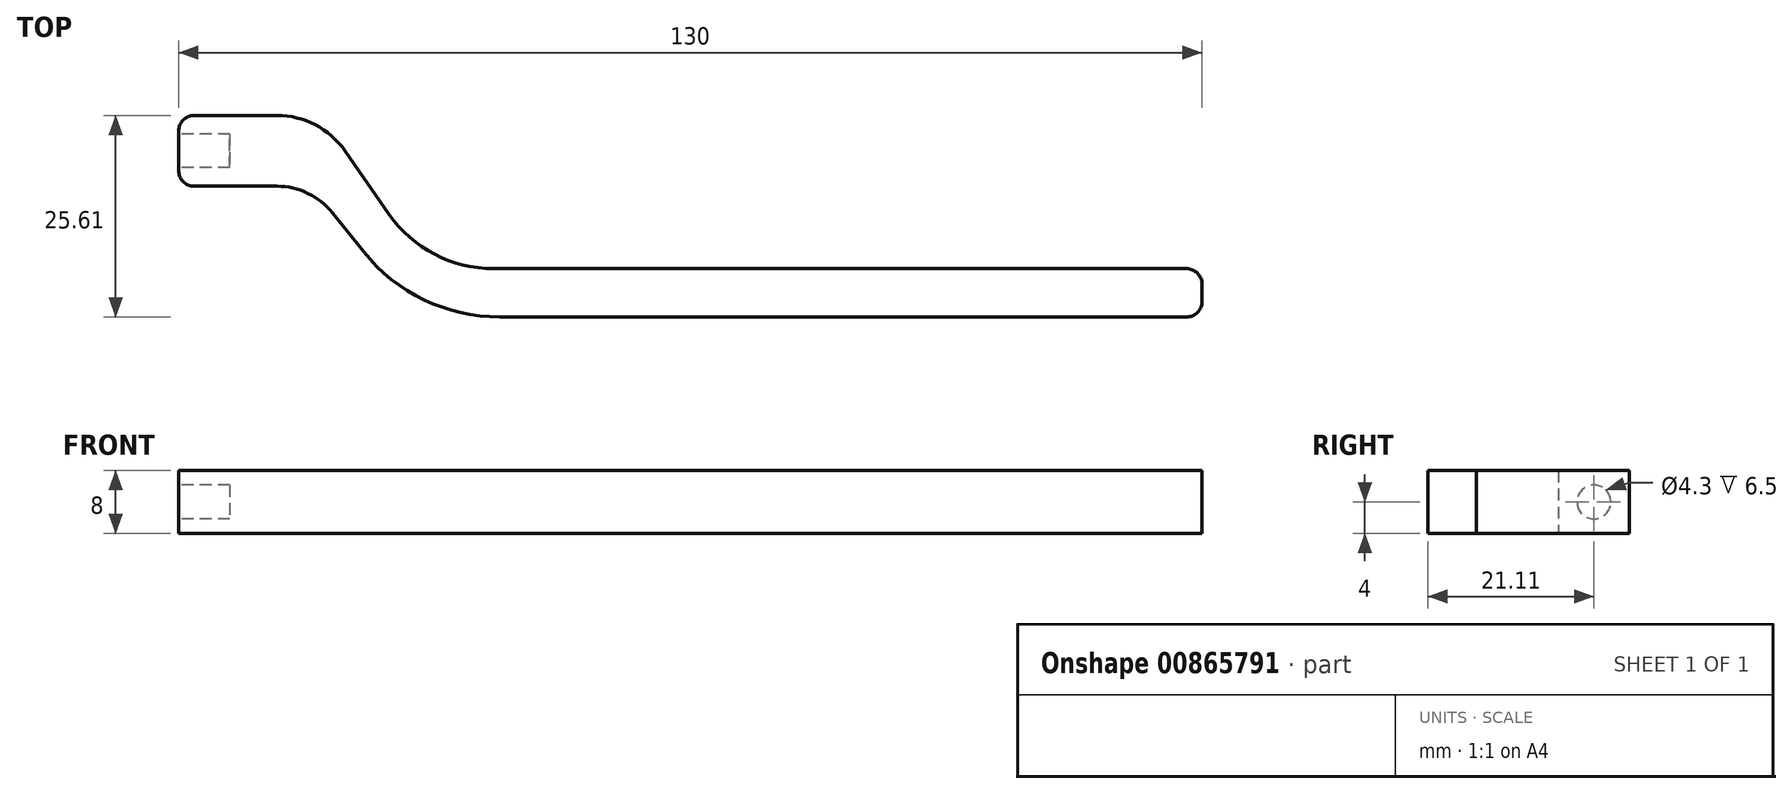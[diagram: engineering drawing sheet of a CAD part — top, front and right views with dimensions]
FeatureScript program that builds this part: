
annotation { "Feature Type Name" : "Feature", "Feature Type Description" : "" }
export const myFeature = defineFeature(function(context is Context, id is Id, definition is map)
    precondition{}
    {
        {
            var Q0;
            Q0=qCreatedBy(makeId("Top.planeOp"),FACE);
            var sketch = newSketch(context, id + "F0", { "sketchPlane" : qUnion([Q0])});
            skLineSegment(sketch, "E0.bottom", {"start": v(6.25, 4.5) * mm, "end": v(-6.25, 4.5) * mm});
            skLineSegment(sketch, "E0.top", {"start": v(6.25, -4.5) * mm, "end": v(-6.25, -4.5) * mm});
            skLineSegment(sketch, "E0.left", {"start": v(6.25, 4.5) * mm, "end": v(6.25, -4.5) * mm});
            skLineSegment(sketch, "E0.right", {"start": v(-6.25, 4.5) * mm, "end": v(-6.25, -4.5) * mm});
            skPoint(sketch, "E0.middle", {"position": v(0, 0) * mm});
            skArc(sketch, "E1", {"start": v(6.25, -4.5) * mm, "mid": v(10.17, -5.4) * mm, "end": v(13.31, -7.9) * mm});
            skLineSegment(sketch, "E2", {"start": v(13.31, -7.9) * mm, "end": v(17.23, -12.8) * mm});
            skArc(sketch, "E3", {"start": v(17.23, -12.8) * mm, "mid": v(24.93, -18.93) * mm, "end": v(34.52, -21.11) * mm});
            skLineSegment(sketch, "E4", {"start": v(34.52, -21.11) * mm, "end": v(123.75, -21.11) * mm});
            skArc(sketch, "E5", {"start": v(6.25, 4.5) * mm, "mid": v(11.11, 3.3) * mm, "end": v(14.87, 0) * mm});
            skLineSegment(sketch, "E6", {"start": v(14.87, 0) * mm, "end": v(20.5, -8.06) * mm});
            skArc(sketch, "E7", {"start": v(20.5, -8.06) * mm, "mid": v(26.26, -13.14) * mm, "end": v(33.72, -14.96) * mm});
            skLineSegment(sketch, "E8", {"start": v(33.72, -14.96) * mm, "end": v(123.75, -14.96) * mm});
            skLineSegment(sketch, "E9", {"start": v(123.75, -14.96) * mm, "end": v(123.75, -21.11) * mm});
            skSolve(sketch);
        }
        {
            var Q0;
            Q0=makeQuery(id+"F0.imprint","IMPRINT",FACE,{"disambiguationData":[TD([[makeQuery(id+"F0.imprint","IMPRINT",EDGE,{"derivedFrom":sQuery(id+"F0.wireOp",EDGE,"E0.bottom")}),1.0]])]});
            var Q1;
            Q1=makeQuery(id+"F0.imprint","IMPRINT",FACE,{"disambiguationData":[TD([[makeQuery(id+"F0.imprint","IMPRINT",EDGE,{"derivedFrom":sQuery(id+"F0.wireOp",EDGE,"E0.left")}),1.0]])]});
            extrude(context, id + "F1", {"entities" : qUnion([Q0, Q1]), "depth" : 8 * mm, "offsetDistance" : 25 * mm});
        }
        {
            var Q0;
            Q0=makeQuery(id+"F1.opExtrude","SWEPT_FACE",FACE,{"disambiguationData":[OSD([sQuery(id+"F0.wireOp",EDGE,"E0.right")])]});
            var sketch = newSketch(context, id + "F2", { "sketchPlane" : qUnion([Q0])});
            skCircle(sketch, "E10", {"center": v(0, 4) * mm, "radius": 2.15 * mm});
            skPoint(sketch, "E10.centerSnap0", {"position": v(-4.5, 4) * mm});
            skSolve(sketch);
        }
        {
            var Q0;
            Q0=makeQuery(id+"F2.imprint","IMPRINT",FACE,{"disambiguationData":[TD([[makeQuery(id+"F2.imprint","IMPRINT",EDGE,{"derivedFrom":sQuery(id+"F2.wireOp",EDGE,"E10")}),1.0]])]});
            extrude(context, id + "F3", {"entities" : qUnion([Q0]), "operationType" : NewBodyOperationType.REMOVE, "oppositeDirection" : true, "depth" : 6.5 * mm, "offsetDistance" : 25 * mm});
        }
        {
            var Q0;
            Q0=makeQuery(id+"F1.opExtrude","SWEPT_EDGE",EDGE,{"disambiguationData":[OSD([sQuery(id+"F0.wireOp",EDGE,"E0.top"),sQuery(id+"F0.wireOp",EDGE,"E0.right")])]});
            var Q1;
            Q1=makeQuery(id+"F1.opExtrude","SWEPT_EDGE",EDGE,{"disambiguationData":[OSD([sQuery(id+"F0.wireOp",EDGE,"E4"),sQuery(id+"F0.wireOp",EDGE,"E9")])]});
            var Q2;
            Q2=makeQuery(id+"F1.opExtrude","SWEPT_EDGE",EDGE,{"disambiguationData":[OSD([sQuery(id+"F0.wireOp",EDGE,"E8"),sQuery(id+"F0.wireOp",EDGE,"E9")])]});
            var Q3;
            Q3=makeQuery(id+"F1.opExtrude","SWEPT_EDGE",EDGE,{"disambiguationData":[OSD([sQuery(id+"F0.wireOp",EDGE,"E0.bottom"),sQuery(id+"F0.wireOp",EDGE,"E0.right")])]});
            fillet(context, id + "F4", {"entities" : qUnion([Q0, Q1, Q2, Q3]), "radius" : 2 * mm, "tangentPropagation" : true, "allowEdgeOverflow" : false});
        }
    });
